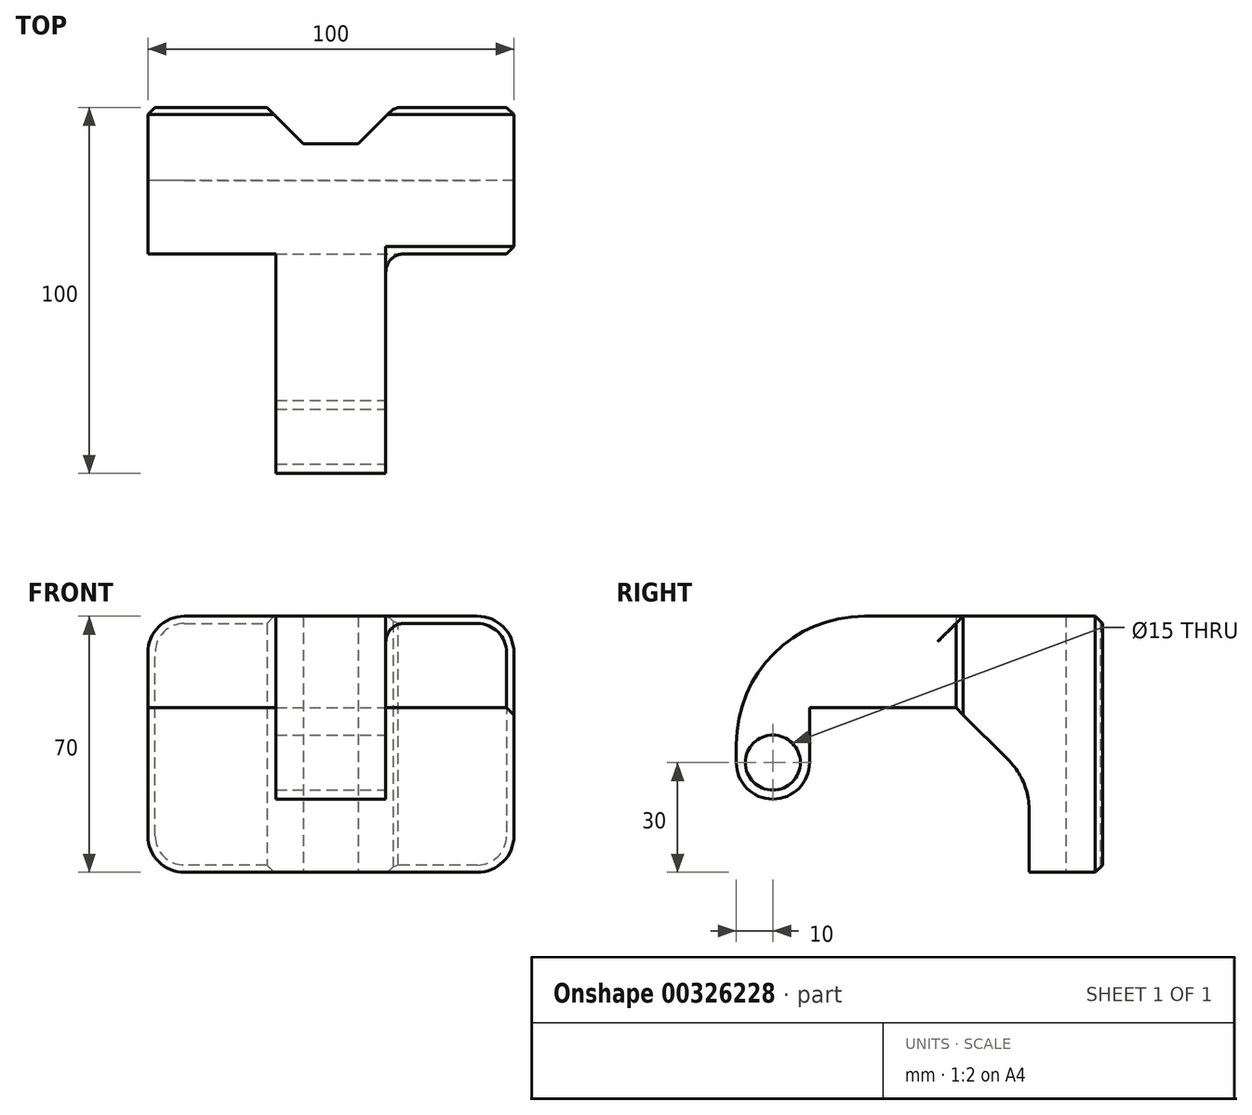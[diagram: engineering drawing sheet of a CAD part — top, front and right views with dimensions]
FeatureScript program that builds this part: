
annotation { "Feature Type Name" : "Feature", "Feature Type Description" : "" }
export const myFeature = defineFeature(function(context is Context, id is Id, definition is map)
    precondition{}
    {
        {
            var Q0;
            Q0=qCreatedBy(makeId("Front.planeOp"),FACE);
            var sketch = newSketch(context, id + "F0", { "sketchPlane" : qUnion([Q0])});
            skLineSegment(sketch, "E0.bottom", {"start": v(50, -35) * mm, "end": v(-50, -35) * mm});
            skLineSegment(sketch, "E0.top", {"start": v(50, 35) * mm, "end": v(-50, 35) * mm});
            skLineSegment(sketch, "E0.left", {"start": v(50, -35) * mm, "end": v(50, 35) * mm});
            skLineSegment(sketch, "E0.right", {"start": v(-50, -35) * mm, "end": v(-50, 35) * mm});
            skPoint(sketch, "E0.middle", {"position": v(0, 0) * mm});
            skSolve(sketch);
        }
        {
            var Q0;
            Q0=makeQuery(id+"F0.imprint","IMPRINT",FACE,{"disambiguationData":[TD([[makeQuery(id+"F0.imprint","IMPRINT",EDGE,{"derivedFrom":sQuery(id+"F0.wireOp",EDGE,"E0.bottom")}),-1.0]])]});
            extrude(context, id + "F1", {"entities" : qUnion([Q0]), "depth" : 40 * mm});
        }
        {
            var Q0;
            Q0=makeQuery(id+"F1.opExtrude","SWEPT_FACE",FACE,{"disambiguationData":[OSD([sQuery(id+"F0.wireOp",EDGE,"E0.left")])]});
            var sketch = newSketch(context, id + "F2", { "sketchPlane" : qUnion([Q0])});
            skLineSegment(sketch, "E1", {"start": v(-20, -35) * mm, "end": v(-20, -10) * mm});
            skLineSegment(sketch, "E2", {"start": v(-20, -10) * mm, "end": v(-40, 10) * mm});
            skLineSegment(sketch, "E3", {"start": v(-40, 10) * mm, "end": v(-40, -35) * mm});
            skLineSegment(sketch, "E4", {"start": v(-40, -35) * mm, "end": v(-20, -35) * mm});
            skSolve(sketch);
        }
        {
            var Q0;
            Q0=makeQuery(id+"F2.imprint","IMPRINT",FACE,{"disambiguationData":[TD([[makeQuery(id+"F2.imprint","IMPRINT",EDGE,{"derivedFrom":sQuery(id+"F2.wireOp",EDGE,"E1")}),1.0]])]});
            extrude(context, id + "F3", {"entities" : qUnion([Q0]), "operationType" : NewBodyOperationType.REMOVE, "endBound" : BoundingType.THROUGH_ALL, "oppositeDirection" : true, "depth" : 25 * mm});
        }
        {
            var Q0;
            Q0=makeQuery(id+"F1.opExtrude","CAP_FACE",FACE,{"disambiguationData":[OSD([sQuery(id+"F0.wireOp",EDGE,"E0.bottom"),sQuery(id+"F0.wireOp",EDGE,"E0.top"),sQuery(id+"F0.wireOp",EDGE,"E0.left"),sQuery(id+"F0.wireOp",EDGE,"E0.right")])],"isStart":false});
            var sketch = newSketch(context, id + "F4", { "sketchPlane" : qUnion([Q0])});
            skLineSegment(sketch, "E5", {"start": v(-15, 35) * mm, "end": v(-15, 10) * mm});
            skLineSegment(sketch, "E6", {"start": v(-15, 10) * mm, "end": v(15, 10) * mm});
            skLineSegment(sketch, "E7", {"start": v(15, 10) * mm, "end": v(15, 35) * mm});
            skLineSegment(sketch, "E8", {"start": v(15, 35) * mm, "end": v(-15, 35) * mm});
            skSolve(sketch);
        }
        {
            var Q0;
            Q0=makeQuery(id+"F4.imprint","IMPRINT",FACE,{"disambiguationData":[TD([[makeQuery(id+"F4.imprint","IMPRINT",EDGE,{"derivedFrom":sQuery(id+"F4.wireOp",EDGE,"E5")}),1.0]])]});
            extrude(context, id + "F5", {"entities" : qUnion([Q0]), "operationType" : NewBodyOperationType.ADD, "depth" : 40 * mm});
        }
        {
            var Q0;
            Q0=makeQuery(id+"F5.opExtrude","SWEPT_FACE",FACE,{"disambiguationData":[OSD([sQuery(id+"F4.wireOp",EDGE,"E7")])]});
            var sketch = newSketch(context, id + "F6", { "sketchPlane" : qUnion([Q0])});
            skLineSegment(sketch, "E9", {"start": v(-80, -15) * mm, "end": v(-100, -15) * mm});
            skLineSegment(sketch, "E10", {"start": v(-100, -15) * mm, "end": v(-100, 35) * mm});
            skLineSegment(sketch, "E11", {"start": v(-100, 35) * mm, "end": v(-80, 35) * mm});
            skLineSegment(sketch, "E12", {"start": v(-80, -15) * mm, "end": v(-80, 35) * mm});
            skSolve(sketch);
        }
        {
            var Q0;
            {var subQ3=sQuery(id+"F6.wireOp",EDGE,"E9");Q0=makeQuery(id+"F6.imprint","IMPRINT",FACE,{"disambiguationData":[TD([[makeQuery(id+"F6.imprint","IMPRINT",EDGE,{"derivedFrom":subQ3}),-1.0]])]});}
            extrude(context, id + "F7", {"entities" : qUnion([Q0]), "operationType" : NewBodyOperationType.ADD, "oppositeDirection" : true, "depth" : 30 * mm});
        }
        {
            var Q0;
            Q0=makeQuery(id+"F1.opExtrude","SWEPT_FACE",FACE,{"disambiguationData":[OSD([sQuery(id+"F0.wireOp",EDGE,"E0.bottom")])]});
            var sketch = newSketch(context, id + "F8", { "sketchPlane" : qUnion([Q0])});
            skLineSegment(sketch, "E13", {"start": v(-17.5, 0) * mm, "end": v(-7.5, 10) * mm});
            skLineSegment(sketch, "E14", {"start": v(-7.5, 10) * mm, "end": v(7.5, 10) * mm});
            skLineSegment(sketch, "E15", {"start": v(7.5, 10) * mm, "end": v(17.5, 0) * mm});
            skLineSegment(sketch, "E16", {"start": v(17.5, 0) * mm, "end": v(-17.5, 0) * mm});
            skSolve(sketch);
        }
        {
            var Q0;
            Q0=makeQuery(id+"F8.imprint","IMPRINT",FACE,{"disambiguationData":[TD([[makeQuery(id+"F8.imprint","IMPRINT",EDGE,{"derivedFrom":sQuery(id+"F8.wireOp",EDGE,"E13")}),-1.0]])]});
            extrude(context, id + "F9", {"entities" : qUnion([Q0]), "operationType" : NewBodyOperationType.REMOVE, "endBound" : BoundingType.THROUGH_ALL, "oppositeDirection" : true, "depth" : 25 * mm});
        }
        {
            var Q0;
            Q0=makeQuery(id+"F7.boolean.opBoolean","MERGE",FACE,{"derivedFrom":[makeQuery(id+"F5.opExtrude","SWEPT_FACE",FACE,{"disambiguationData":[OSD([sQuery(id+"F4.wireOp",EDGE,"E7")])]}),makeQuery(id+"F7.opExtrude","CAP_FACE",FACE,{"disambiguationData":[OSD([sQuery(id+"F6.wireOp",EDGE,"E9"),sQuery(id+"F6.wireOp",EDGE,"E10"),sQuery(id+"F6.wireOp",EDGE,"E11"),sQuery(id+"F6.wireOp",EDGE,"E12")])],"isStart":true})]});
            var sketch = newSketch(context, id + "F10", { "sketchPlane" : qUnion([Q0])});
            skCircle(sketch, "E17", {"center": v(-90, -5) * mm, "radius": 7.5 * mm});
            skPoint(sketch, "E17.centerSnap0", {"position": v(-90, -15) * mm});
            skSolve(sketch);
        }
        {
            var Q0;
            Q0=makeQuery(id+"F10.imprint","IMPRINT",FACE,{"disambiguationData":[TD([[makeQuery(id+"F10.imprint","IMPRINT",EDGE,{"derivedFrom":sQuery(id+"F10.wireOp",EDGE,"E17")}),1.0]])]});
            extrude(context, id + "F11", {"entities" : qUnion([Q0]), "operationType" : NewBodyOperationType.REMOVE, "endBound" : BoundingType.THROUGH_ALL, "oppositeDirection" : true, "depth" : 25 * mm});
        }
        {
            var Q0;
            Q0=makeQuery(id+"F7.opExtrude","SWEPT_EDGE",EDGE,{"disambiguationData":[OSD([sQuery(id+"F6.wireOp",EDGE,"E9"),sQuery(id+"F6.wireOp",EDGE,"E10")])]});
            var Q1;
            Q1=makeQuery(id+"F7.opExtrude","SWEPT_EDGE",EDGE,{"disambiguationData":[OSD([sQuery(id+"F6.wireOp",EDGE,"E9"),sQuery(id+"F6.wireOp",EDGE,"E12")])]});
            var Q2;
            Q2=makeQuery(id+"F5.opExtrude","CAP_EDGE",EDGE,{"disambiguationData":[OSD([sQuery(id+"F4.wireOp",EDGE,"E6")])],"isStart":false});
            fillet(context, id + "F12", {"entities" : qUnion([Q0, Q1, Q2]), "radius" : 10 * mm, "tangentPropagation" : true, "allowEdgeOverflow" : false});
        }
        {
            var Q0;
            Q0=makeQuery(id+"F7.opExtrude","SWEPT_EDGE",EDGE,{"disambiguationData":[OSD([sQuery(id+"F6.wireOp",EDGE,"E10"),sQuery(id+"F6.wireOp",EDGE,"E11")])]});
            fillet(context, id + "F13", {"entities" : qUnion([Q0]), "radius" : 35 * mm, "tangentPropagation" : true, "allowEdgeOverflow" : false});
        }
        {
            var Q0;
            Q0=makeQuery(id+"F1.opExtrude","SWEPT_EDGE",EDGE,{"disambiguationData":[OSD([sQuery(id+"F0.wireOp",EDGE,"E0.bottom"),sQuery(id+"F0.wireOp",EDGE,"E0.left")])]});
            var Q1;
            Q1=makeQuery(id+"F1.opExtrude","SWEPT_EDGE",EDGE,{"disambiguationData":[OSD([sQuery(id+"F0.wireOp",EDGE,"E0.bottom"),sQuery(id+"F0.wireOp",EDGE,"E0.right")])]});
            var Q2;
            Q2=makeQuery(id+"F1.opExtrude","SWEPT_EDGE",EDGE,{"disambiguationData":[OSD([sQuery(id+"F0.wireOp",EDGE,"E0.top"),sQuery(id+"F0.wireOp",EDGE,"E0.right")])]});
            var Q3;
            Q3=makeQuery(id+"F1.opExtrude","SWEPT_EDGE",EDGE,{"disambiguationData":[OSD([sQuery(id+"F0.wireOp",EDGE,"E0.top"),sQuery(id+"F0.wireOp",EDGE,"E0.left")])]});
            fillet(context, id + "F14", {"entities" : qUnion([Q0, Q1, Q2, Q3]), "radius" : 10 * mm, "tangentPropagation" : true, "allowEdgeOverflow" : false});
        }
        {
            var Q0;
            Q0=makeQuery(id+"F3.boolean.opBoolean","COPY",EDGE,{"derivedFrom":makeQuery(id+"F3.opExtrude","SWEPT_EDGE",EDGE,{"disambiguationData":[OSD([sQuery(id+"F2.wireOp",EDGE,"E1"),sQuery(id+"F2.wireOp",EDGE,"E2")])]})});
            fillet(context, id + "F15", {"entities" : qUnion([Q0]), "radius" : 20 * mm, "tangentPropagation" : true, "rho" : 0.5, "crossSection" : FilletCrossSection.CONIC, "allowEdgeOverflow" : false});
        }
        {
            var Q0;
            Q0=makeQuery(id+"F3.boolean.opBoolean","COPY",EDGE,{"derivedFrom":makeQuery(id+"F3.opExtrude","SWEPT_EDGE",EDGE,{"disambiguationData":[OSD([sQuery(id+"F0.wireOp",EDGE,"E0.bottom"),sQuery(id+"F0.wireOp",EDGE,"E0.left"),sQuery(id+"F2.wireOp",EDGE,"E1"),sQuery(id+"F2.wireOp",EDGE,"E4")])]})});
            var Q1;
            Q1=makeQuery(id+"F1.opExtrude","CAP_EDGE",EDGE,{"disambiguationData":[OSD([sQuery(id+"F0.wireOp",EDGE,"E0.left")])],"isStart":false});
            var Q2;
            {var subQ0=sQuery(id+"F2.wireOp",EDGE,"E2");var subQ1=sQuery(id+"F0.wireOp",EDGE,"E0.left");Q2=makeQuery(id+"F5.boolean.opBoolean","SPLIT",EDGE,{"disambiguationData":[TD([makeQuery(id+"F1.opExtrude","SWEPT_FACE",FACE,{"disambiguationData":[OSD([subQ1])]})])],"derivedFrom":makeQuery(id+"F3.boolean.opBoolean","COPY",EDGE,{"derivedFrom":makeQuery(id+"F3.opExtrude","SWEPT_EDGE",EDGE,{"disambiguationData":[OSD([subQ1,subQ0,sQuery(id+"F2.wireOp",EDGE,"E3")])]})})});}
            var Q3;
            {var subQ0=sQuery(id+"F2.wireOp",EDGE,"E2");var subQ1=sQuery(id+"F0.wireOp",EDGE,"E0.right");var subQ2=sQuery(id+"F0.wireOp",EDGE,"E0.left");Q3=makeQuery(id+"F5.boolean.opBoolean","SPLIT",EDGE,{"disambiguationData":[TD([makeQuery(id+"F1.opExtrude","SWEPT_FACE",FACE,{"disambiguationData":[OSD([subQ1])]})])],"derivedFrom":makeQuery(id+"F3.boolean.opBoolean","COPY",EDGE,{"derivedFrom":makeQuery(id+"F3.opExtrude","SWEPT_EDGE",EDGE,{"disambiguationData":[OSD([subQ2,subQ0,sQuery(id+"F2.wireOp",EDGE,"E3")])]})})});}
            chamfer(context, id + "F16", {"entities" : qUnion([Q0, Q1, Q2, Q3]), "width" : 2 * mm, "tangentPropagation" : true});
        }
        {
            var Q0;
            Q0=makeQuery(id+"F5.opExtrude","CAP_EDGE",EDGE,{"disambiguationData":[OSD([sQuery(id+"F4.wireOp",EDGE,"E7")])],"isStart":true});
            var Q1;
            Q1=makeQuery(id+"F5.opExtrude","CAP_EDGE",EDGE,{"disambiguationData":[OSD([sQuery(id+"F4.wireOp",EDGE,"E5")])],"isStart":true});
            fillet(context, id + "F17", {"entities" : qUnion([Q0, Q1]), "radius" : 5 * mm, "tangentPropagation" : true, "allowEdgeOverflow" : false});
        }
        {
            var Q0;
            {var subQ0=sQuery(id+"F0.wireOp",EDGE,"E0.bottom");var subQ1=sQuery(id+"F0.wireOp",EDGE,"E0.left");Q0=makeQuery(id+"F9.boolean.opBoolean","SPLIT",EDGE,{"disambiguationData":[TD([makeQuery(id+"F1.opExtrude","SWEPT_FACE",FACE,{"disambiguationData":[OSD([subQ1])]})])],"derivedFrom":makeQuery(id+"F1.opExtrude","CAP_EDGE",EDGE,{"disambiguationData":[OSD([subQ0])],"isStart":true})});}
            var Q1;
            {var subQ0=sQuery(id+"F0.wireOp",EDGE,"E0.bottom");var subQ1=sQuery(id+"F0.wireOp",EDGE,"E0.right");Q1=makeQuery(id+"F9.boolean.opBoolean","SPLIT",EDGE,{"disambiguationData":[TD([makeQuery(id+"F1.opExtrude","SWEPT_FACE",FACE,{"disambiguationData":[OSD([subQ1])]})])],"derivedFrom":makeQuery(id+"F1.opExtrude","CAP_EDGE",EDGE,{"disambiguationData":[OSD([subQ0])],"isStart":true})});}
            var Q2;
            Q2=makeQuery(id+"F9.boolean.opBoolean","COPY",EDGE,{"derivedFrom":makeQuery(id+"F9.opExtrude","SWEPT_EDGE",EDGE,{"disambiguationData":[OSD([sQuery(id+"F0.wireOp",EDGE,"E0.bottom"),sQuery(id+"F8.wireOp",EDGE,"E13"),sQuery(id+"F8.wireOp",EDGE,"E16")])]})});
            var Q3;
            Q3=makeQuery(id+"F9.boolean.opBoolean","COPY",EDGE,{"derivedFrom":makeQuery(id+"F9.opExtrude","SWEPT_EDGE",EDGE,{"disambiguationData":[OSD([sQuery(id+"F0.wireOp",EDGE,"E0.bottom"),sQuery(id+"F8.wireOp",EDGE,"E15"),sQuery(id+"F8.wireOp",EDGE,"E16")])]})});
            chamfer(context, id + "F18", {"entities" : qUnion([Q0, Q1, Q2, Q3]), "width" : 2 * mm, "tangentPropagation" : true});
        }
    });
